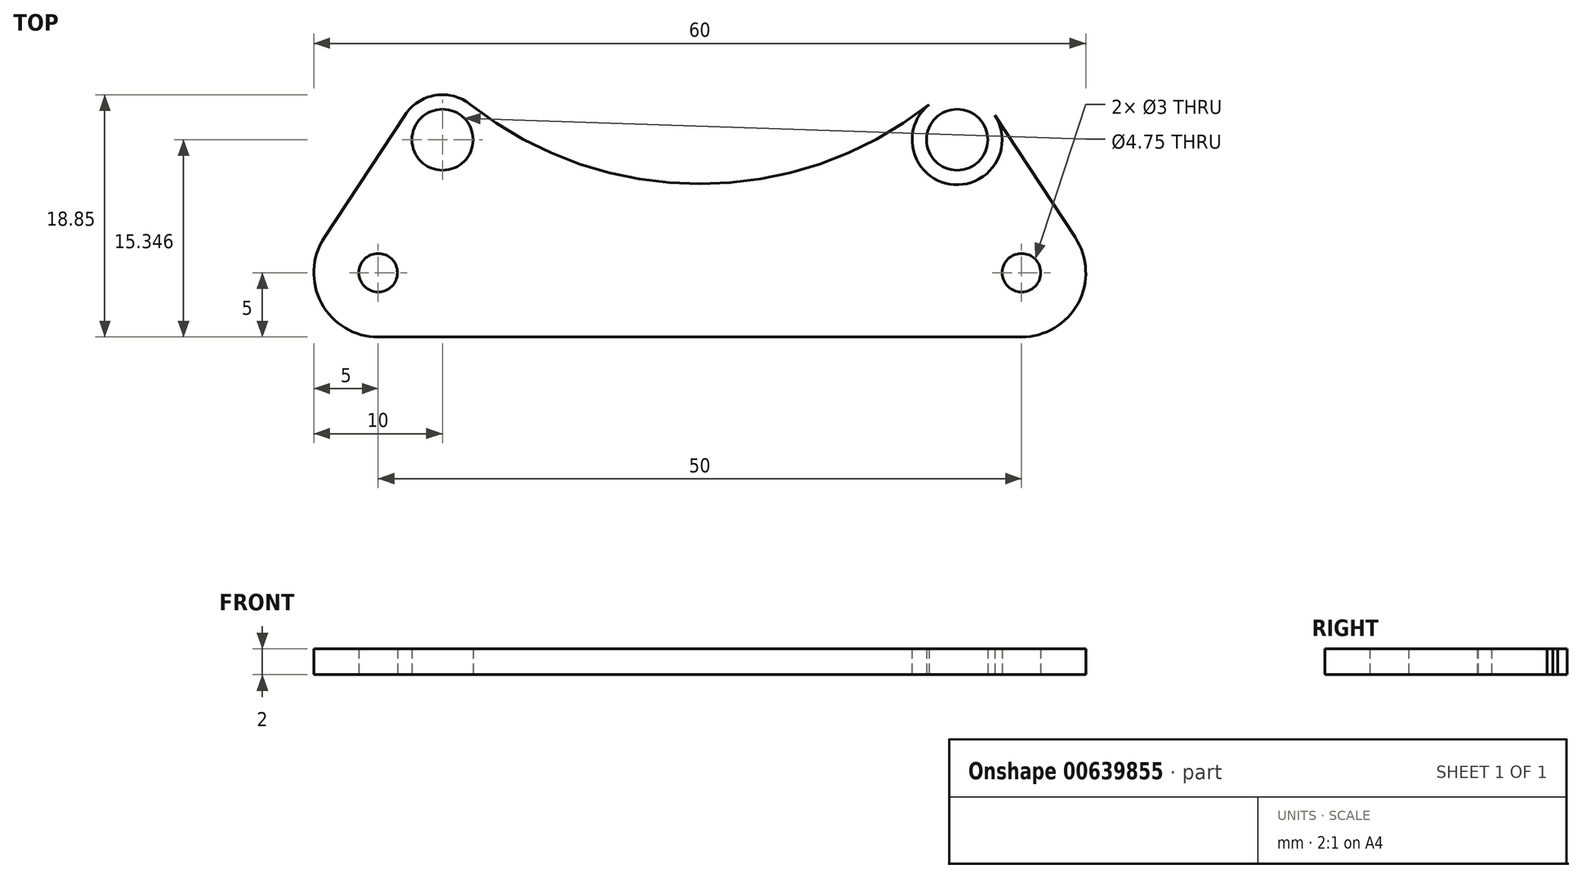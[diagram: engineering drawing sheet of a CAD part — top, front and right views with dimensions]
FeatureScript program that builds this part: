
annotation { "Feature Type Name" : "Feature", "Feature Type Description" : "" }
export const myFeature = defineFeature(function(context is Context, id is Id, definition is map)
    precondition{}
    {
        {
            var Q0;
            Q0=qCreatedBy(makeId("Top.planeOp"),FACE);
            var sketch = newSketch(context, id + "F0", { "sketchPlane" : qUnion([Q0])});
            skCircle(sketch, "E0", {"center": v(-25, 0) * mm, "radius": 1.5 * mm});
            skCircle(sketch, "E1", {"center": v(25, 0) * mm, "radius": 1.5 * mm});
            skCircle(sketch, "E2", {"center": v(-25, 0) * mm, "radius": 5 * mm});
            skCircle(sketch, "E3", {"center": v(25, 0) * mm, "radius": 5 * mm});
            skCircle(sketch, "E4", {"center": v(-20, 10.35) * mm, "radius": 2.38 * mm});
            skLineSegment(sketch, "E5", {"start": v(-25.57, 4.97) * mm, "end": v(25, 5) * mm, "construction": true});
            skCircle(sketch, "E6.MirrorC", {"center": v(20, 10.35) * mm, "radius": 2.38 * mm});
            skCircle(sketch, "E7", {"center": v(-20, 10.35) * mm, "radius": 3.5 * mm});
            skCircle(sketch, "E8.MirrorC", {"center": v(20, 10.35) * mm, "radius": 3.5 * mm});
            skLineSegment(sketch, "E9", {"start": v(-29.18, 2.74) * mm, "end": v(-22.93, 12.27) * mm});
            skLineSegment(sketch, "E10", {"start": v(-25, -5) * mm, "end": v(25, -5) * mm});
            skLineSegment(sketch, "E11", {"start": v(22.93, 12.27) * mm, "end": v(29.18, 2.74) * mm});
            skArc(sketch, "E12", {"start": v(-17.83, 13.1) * mm, "mid": v(0.15, 6.9) * mm, "end": v(18.06, 13.28) * mm});
            skSolve(sketch);
        }
        {
            var Q0;
            Q0=makeQuery(id+"F0.imprint","IMPRINT",FACE,{"disambiguationData":[TD([[makeQuery(id+"F0.imprint","IMPRINT",EDGE,{"derivedFrom":sQuery(id+"F0.wireOp",EDGE,"E0")}),-1.0]])]});
            var Q1;
            {var subQ4=sQuery(id+"F0.wireOp",EDGE,"E9");Q1=makeQuery(id+"F0.imprint","IMPRINT",FACE,{"disambiguationData":[TD([[makeQuery(id+"F0.imprint","IMPRINT",EDGE,{"derivedFrom":subQ4}),-1.0]])]});}
            var Q2;
            Q2=makeQuery(id+"F0.imprint","IMPRINT",FACE,{"disambiguationData":[TD([[makeQuery(id+"F0.imprint","IMPRINT",EDGE,{"derivedFrom":sQuery(id+"F0.wireOp",EDGE,"E1")}),-1.0]])]});
            var Q3;
            Q3=makeQuery(id+"F0.imprint","IMPRINT",FACE,{"disambiguationData":[TD([[makeQuery(id+"F0.imprint","IMPRINT",EDGE,{"derivedFrom":sQuery(id+"F0.wireOp",EDGE,"E6.MirrorC")}),1.0]])]});
            var Q4;
            Q4=makeQuery(id+"F0.imprint","IMPRINT",FACE,{"disambiguationData":[TD([[makeQuery(id+"F0.imprint","IMPRINT",EDGE,{"derivedFrom":sQuery(id+"F0.wireOp",EDGE,"E4")}),-1.0]])]});
            extrude(context, id + "F1", {"entities" : qUnion([Q0, Q1, Q2, Q3, Q4]), "depth" : 2 * mm, "offsetDistance" : 25 * mm});
        }
    });
